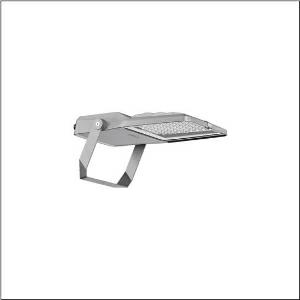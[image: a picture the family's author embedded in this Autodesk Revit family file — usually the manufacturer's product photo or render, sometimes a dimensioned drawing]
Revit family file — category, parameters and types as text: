
# Revit family: floodlight_fl_21_iq_mini___pl52_5xa7771b4d1a_5516
name_source: partatom
category: Lighting Fixtures
units: mm (PartAtom-declared; Revit-internal decimal feet)

## family parameters
Cut with Voids When Loaded = No
Host = Face
Light Source = No
Part Type = Normal
Room Calculation Point = No
Round Connector Dimension = Use Diameter
Shared = No

## types (1)
- --- (1 x LED, 6490 lm, 45.5 W, 4000K)
    Apparent Load = 46 VA
    CIE Flux Codes = 26 60 98 100 100
    Color Rendering = 70
    Color Temperature = 4000K
    Default Elevation = 1800 mm
    Description = Floodlight FL 21 iQ mini, floodlight, primary light control with lens, of PMMA, primary optical cover: protective disc, of toughened safety glass, transparent, light distribution: PL52, light emission: direct distribution, installation type: surface-mounted, lamps: LED, High Power LED, rated values: 6.490lm | 45,5W | 142,6lm/W (begin service life); end service life: 6.490lm | 48W; at 50% lumin. flux: 3.245lm | 21,5W | 150,9lm/W, colour temperature: 4000K, colour rendering: CRI > 70, light colour: 740, light setting 1 begin service life: 100% | 6.490lm | 45,5W | 142,6lm/W | 4.000K, light setting 1 end service life: 48W, further light settings possible, control: Auto-Match, Temp-Guard, Lumen-Switch, Night-Set, Smart-Wire, Light-Fading, Desk-Remote (wireless, voltage-free reading and setting of iQ features in the workshop via application-optimized NFC function/RFID function), optimised constant luminous flux control (CLO 2.0), pre-setting: linear dimming characteristic, with terminal, 6-pole, mains connection: 220..240V, AC, 50/60Hz, luminaire housing, of diecast aluminium, powder-coated, SITECO metallic grey (DB 702S), corrosivity category C5 mid according to DIN EN ISO 12944suitable for swimming poolschlorine-resistant, sealing non-destructively replaceable, mounting bracket, of steel, galvanised, powder-coated, SITECO metallic grey (DB 702S), protection rating (complete): IP66, insulation class (complete): insulation class II (safety insulation), certification: CE, ENEC, VDE, protection symbol: D, impact resistance: IK08, permissible operating ambient temperature: -40..+40°C, permissible operating ambient temperature for outdoor applications: -40..+50°C, standard: DIN EN 12944, LABS conformity tested according to VDMA 24364:2018-05, packaging unit: 1 piece

Light Distribution: PL52
    Height = 70 mm
    Lamp = 1 x LED
    Lamp Light Flux = 6490 lm
    Lamp Power = 45.5 W
    Lamp count = 1
    Length = 485 mm
    Luminous efficacy = 143 lm/W
    Manufacturer = Siteco
    ModVariant = No
    Model = 5XA7771B4D1A
    Mounting Place = Wall
    Mounting Type = Surface mounted
    Number of Poles = 1
    OnlyDefault = Yes
    Power Factor = 1
    Product Name = Floodlight FL 21 iQ mini | PL52
    Product group = floodlight | wall mounted
    ProductGroupID = 2002
    Protection Class = Protection class II
    Protection Degree = IP 66
    RLX_Detail_Level = 1
    RLX_Emergency_Light_Flux = 0 lm
    RLX_Emergency_Type = 0
    RLX_Emergency_Type_DB = No
    RlxData = <blob elided: 96653 chars, md5=6b5e7243>
    Socket = socket
    Standby Power = 0 W
    System Light Flux = 6490 lm
    System Power = 46 W
    Type Comments = factory setting: luminous flux: 100 % | dim-lin: 254 | 463 mA
    Type Image = l_1006845.jpg
    URL = http://relux.com
    VarID = @adj_164529
    Voltage = 0 V
    Weight = 0.00 kg
    Width = 337 mm

## geometry (parser evidence)
native form markers: Blend x4, Sweep x11
no freeform markers — native parametric forms only
